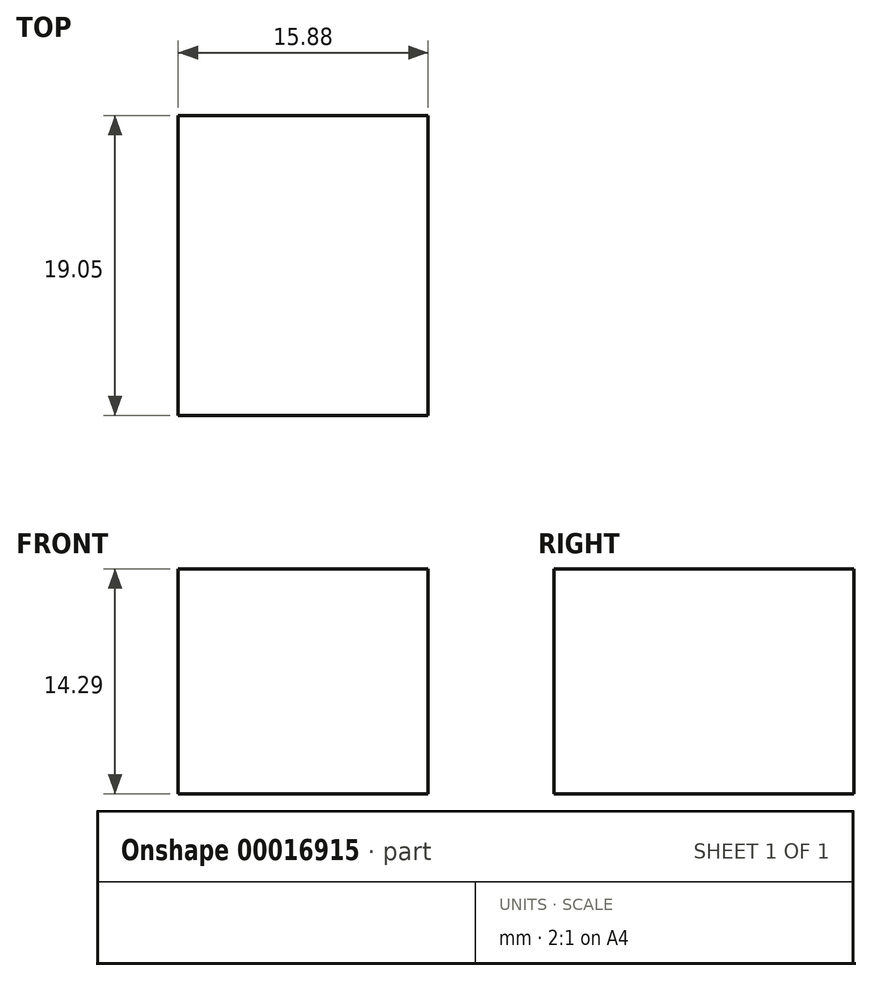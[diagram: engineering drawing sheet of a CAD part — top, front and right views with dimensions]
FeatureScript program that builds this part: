
annotation { "Feature Type Name" : "Feature", "Feature Type Description" : "" }
export const myFeature = defineFeature(function(context is Context, id is Id, definition is map)
    precondition{}
    {
        {
            var Q0;
            Q0=qCreatedBy(makeId("Front.planeOp"),FACE);
            var sketch = newSketch(context, id + "F0", { "sketchPlane" : qUnion([Q0])});
            skLineSegment(sketch, "E0.bottom", {"start": v(0, 0) * mm, "end": v(15.88, 0) * mm});
            skLineSegment(sketch, "E0.top", {"start": v(0, 19.05) * mm, "end": v(15.87, 19.05) * mm});
            skLineSegment(sketch, "E0.left", {"start": v(0, 0) * mm, "end": v(0, 19.05) * mm});
            skLineSegment(sketch, "E0.right", {"start": v(15.88, 0) * mm, "end": v(15.87, 19.05) * mm});
            skSolve(sketch);
        }
        {
            var Q0;
            Q0=makeQuery(id+"F0.imprint","IMPRINT",FACE,{"disambiguationData":[TD([[makeQuery(id+"F0.imprint","IMPRINT",EDGE,{"derivedFrom":sQuery(id+"F0.wireOp",EDGE,"E0.bottom")}),1.0]])]});
            extrude(context, id + "F1", {"entities" : qUnion([Q0]), "depth" : 14.29 * mm});
        }
        {
            var Q0;
            Q0=makeQuery(id+"F1.opExtrude","SWEPT_BODY",BODY,{"disambiguationData":[OSD([sQuery(id+"F0.wireOp",EDGE,"E0.bottom"),sQuery(id+"F0.wireOp",EDGE,"E0.top"),sQuery(id+"F0.wireOp",EDGE,"E0.left"),sQuery(id+"F0.wireOp",EDGE,"E0.right")])]});
            var Q1;
            Q1=makeQuery(id+"F1.opExtrude","CAP_EDGE",EDGE,{"disambiguationData":[OSD([sQuery(id+"F0.wireOp",EDGE,"E0.bottom")])],"isStart":true});
            transform(context, id + "F2", {"entities" : qUnion([Q0]), "transformType" : TransformType.ROTATION, "transformAxis" : qUnion([Q1]), "angle" : 90 * degree, "makeCopy" : false});
        }
    });
